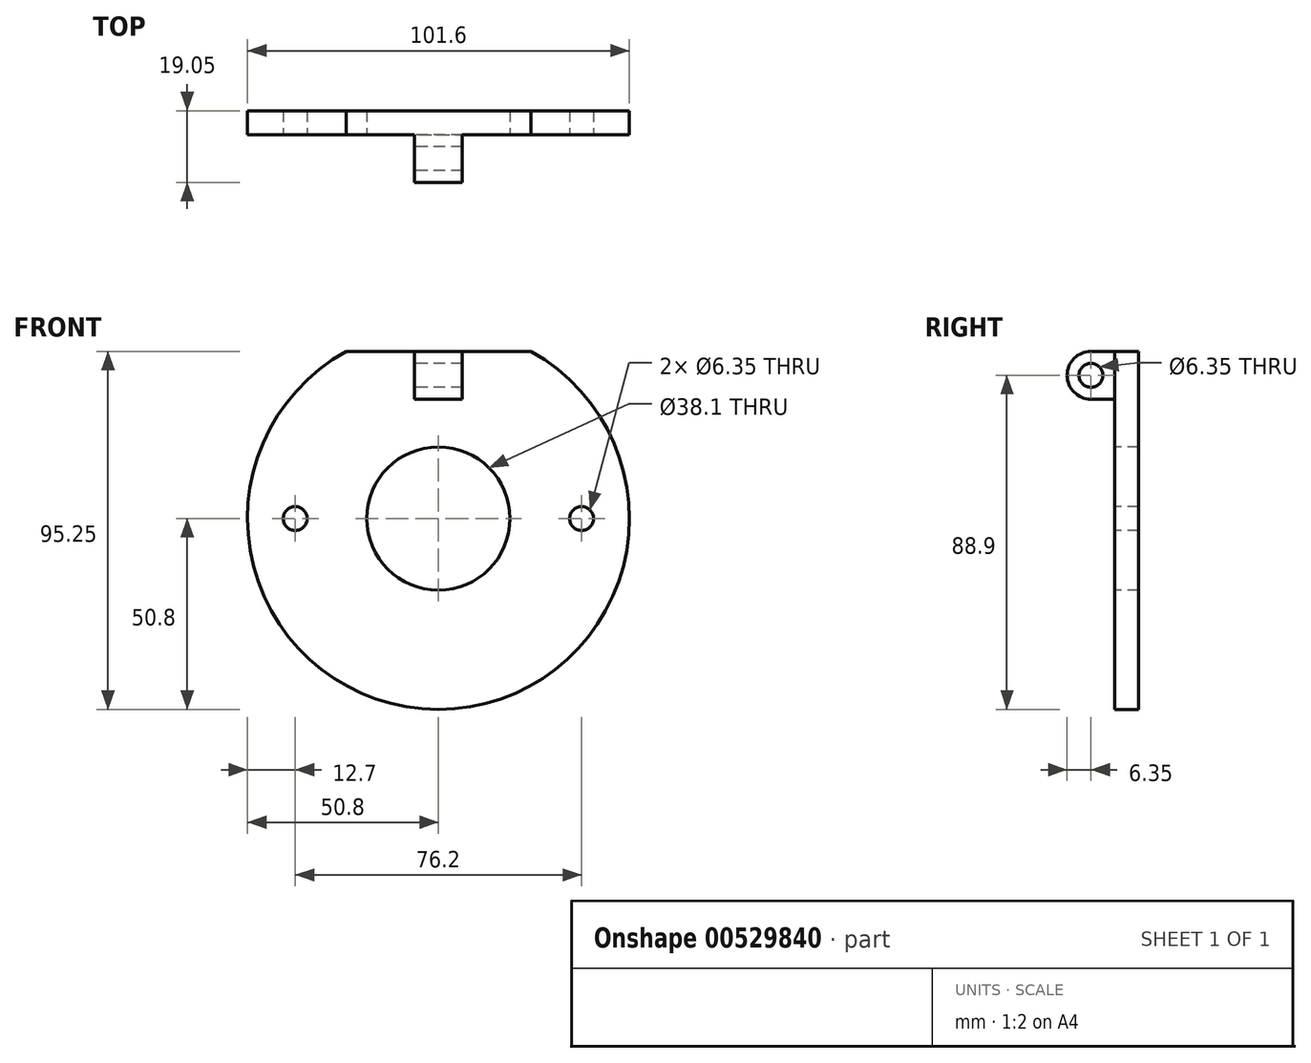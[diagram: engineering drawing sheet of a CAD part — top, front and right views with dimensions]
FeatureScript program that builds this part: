
annotation { "Feature Type Name" : "Feature", "Feature Type Description" : "" }
export const myFeature = defineFeature(function(context is Context, id is Id, definition is map)
    precondition{}
    {
        {
            var Q0;
            Q0=qCreatedBy(makeId("Front.planeOp"),FACE);
            var sketch = newSketch(context, id + "F0", { "sketchPlane" : qUnion([Q0])});
            skCircle(sketch, "E0", {"center": v(0, 0) * mm, "radius": 50.8 * mm});
            skSolve(sketch);
        }
        {
            var Q0;
            Q0 = qSketchRegion(id + "F0", true);
            extrude(context, id + "F1", {"entities" : qUnion([Q0]), "depth" : 6.35 * mm, "offsetDistance" : 25.4 * mm});
        }
        {
            var Q0;
            Q0=makeQuery(id+"F1.opExtrude","CAP_FACE",FACE,{"disambiguationData":[OSD([sQuery(id+"F0.wireOp",EDGE,"E0")])],"isStart":false});
            var sketch = newSketch(context, id + "F2", { "sketchPlane" : qUnion([Q0])});
            skLineSegment(sketch, "E1.bottom", {"start": v(6.35, 31.75) * mm, "end": v(-6.35, 31.75) * mm});
            skLineSegment(sketch, "E1.top", {"start": v(6.35, 44.45) * mm, "end": v(-6.35, 44.45) * mm});
            skLineSegment(sketch, "E1.left", {"start": v(6.35, 31.75) * mm, "end": v(6.35, 44.45) * mm});
            skLineSegment(sketch, "E1.right", {"start": v(-6.35, 31.75) * mm, "end": v(-6.35, 44.45) * mm});
            skPoint(sketch, "E1.middle", {"position": v(0, 38.1) * mm});
            skSolve(sketch);
        }
        {
            var Q0;
            Q0 = qSketchRegion(id + "F2", true);
            extrude(context, id + "F3", {"entities" : qUnion([Q0]), "operationType" : NewBodyOperationType.ADD, "depth" : 12.7 * mm, "offsetDistance" : 25.4 * mm});
        }
        {
            var Q0;
            Q0=makeQuery(id+"F3.opExtrude","CAP_EDGE",EDGE,{"disambiguationData":[OSD([sQuery(id+"F2.wireOp",EDGE,"E1.bottom")])],"isStart":false});
            var Q1;
            Q1=makeQuery(id+"F3.opExtrude","CAP_EDGE",EDGE,{"disambiguationData":[OSD([sQuery(id+"F2.wireOp",EDGE,"E1.top")])],"isStart":false});
            fillet(context, id + "F4", {"entities" : qUnion([Q0, Q1]), "radius" : 6.35 * mm, "tangentPropagation" : true, "allowEdgeOverflow" : false});
        }
        {
            var Q0;
            Q0=makeQuery(id+"F3.opExtrude","SWEPT_FACE",FACE,{"disambiguationData":[OSD([sQuery(id+"F2.wireOp",EDGE,"E1.right")])]});
            var sketch = newSketch(context, id + "F5", { "sketchPlane" : qUnion([Q0])});
            skCircle(sketch, "E2", {"center": v(12.7, 38.1) * mm, "radius": 3.18 * mm});
            skSolve(sketch);
        }
        {
            var Q0;
            Q0=makeQuery(id+"F5.imprint","IMPRINT",FACE,{"disambiguationData":[TD([[makeQuery(id+"F5.imprint","IMPRINT",EDGE,{"derivedFrom":sQuery(id+"F5.wireOp",EDGE,"E2")}),1.0]])]});
            extrude(context, id + "F6", {"entities" : qUnion([Q0]), "operationType" : NewBodyOperationType.REMOVE, "endBound" : BoundingType.THROUGH_ALL, "oppositeDirection" : true, "depth" : 25.4 * mm, "offsetDistance" : 25.4 * mm});
        }
        {
            var Q0;
            Q0=makeQuery(id+"F1.opExtrude","CAP_FACE",FACE,{"disambiguationData":[OSD([sQuery(id+"F0.wireOp",EDGE,"E0")])],"isStart":false});
            var sketch = newSketch(context, id + "F7", { "sketchPlane" : qUnion([Q0])});
            skCircle(sketch, "E3", {"center": v(-38.1, 0) * mm, "radius": 3.18 * mm});
            skCircle(sketch, "E4", {"center": v(38.1, 0) * mm, "radius": 3.18 * mm});
            skCircle(sketch, "E5", {"center": v(0, 0) * mm, "radius": 19.05 * mm});
            skSolve(sketch);
        }
        {
            var Q0;
            Q0 = qSketchRegion(id + "F7", true);
            extrude(context, id + "F8", {"entities" : qUnion([Q0]), "operationType" : NewBodyOperationType.REMOVE, "endBound" : BoundingType.THROUGH_ALL, "oppositeDirection" : true, "depth" : 25.4 * mm, "offsetDistance" : 25.4 * mm});
        }
        {
            var Q0;
            Q0=makeQuery(id+"F1.opExtrude","CAP_FACE",FACE,{"disambiguationData":[OSD([sQuery(id+"F0.wireOp",EDGE,"E0")])],"isStart":false});
            var sketch = newSketch(context, id + "F9", { "sketchPlane" : qUnion([Q0])});
            skLineSegment(sketch, "E6", {"start": v(6.35, 44.45) * mm, "end": v(24.6, 44.45) * mm});
            skLineSegment(sketch, "E7", {"start": v(6.35, 44.45) * mm, "end": v(-24.6, 44.45) * mm});
            skArc(sketch, "E8.0", {"start": v(24.6, 44.45) * mm, "mid": v(0, 50.8) * mm, "end": v(-24.6, 44.45) * mm});
            skSolve(sketch);
        }
        {
            var Q0;
            Q0 = qSketchRegion(id + "F9", true);
            extrude(context, id + "F10", {"entities" : qUnion([Q0]), "operationType" : NewBodyOperationType.REMOVE, "endBound" : BoundingType.THROUGH_ALL, "oppositeDirection" : true, "depth" : 25.4 * mm, "offsetDistance" : 25.4 * mm});
        }
    });
